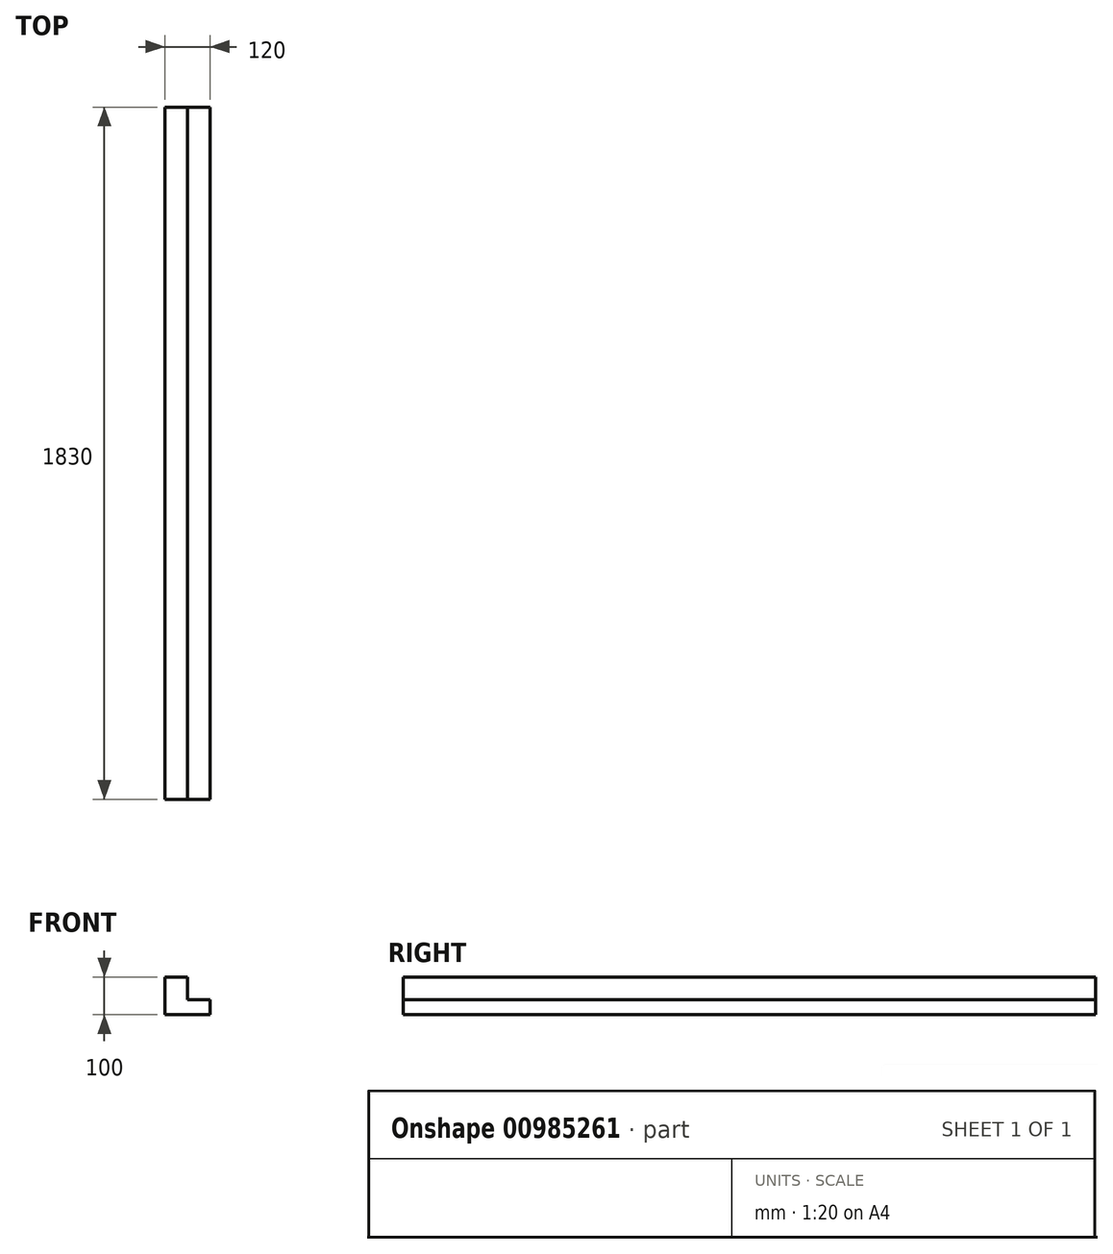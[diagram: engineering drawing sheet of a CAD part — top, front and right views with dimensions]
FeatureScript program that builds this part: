
annotation { "Feature Type Name" : "Feature", "Feature Type Description" : "" }
export const myFeature = defineFeature(function(context is Context, id is Id, definition is map)
    precondition{}
    {
        {
            var Q0;
            Q0=qCreatedBy(makeId("Front.planeOp"),FACE);
            var sketch = newSketch(context, id + "F0", { "sketchPlane" : qUnion([Q0])});
            skLineSegment(sketch, "E0", {"start": v(0, 0) * mm, "end": v(0, 100) * mm});
            skLineSegment(sketch, "E1", {"start": v(0, 100) * mm, "end": v(60, 100) * mm});
            skLineSegment(sketch, "E2", {"start": v(60, 100) * mm, "end": v(60, 40) * mm});
            skLineSegment(sketch, "E3", {"start": v(60, 40) * mm, "end": v(120, 40) * mm});
            skLineSegment(sketch, "E4", {"start": v(120, 40) * mm, "end": v(120, 0) * mm});
            skLineSegment(sketch, "E5", {"start": v(120, 0) * mm, "end": v(0, 0) * mm});
            skSolve(sketch);
        }
        {
            var Q0;
            Q0 = qSketchRegion(id + "F0", true);
            extrude(context, id + "F1", {"entities" : qUnion([Q0]), "depth" : 1830 * mm, "offsetDistance" : 25 * mm});
        }
    });
